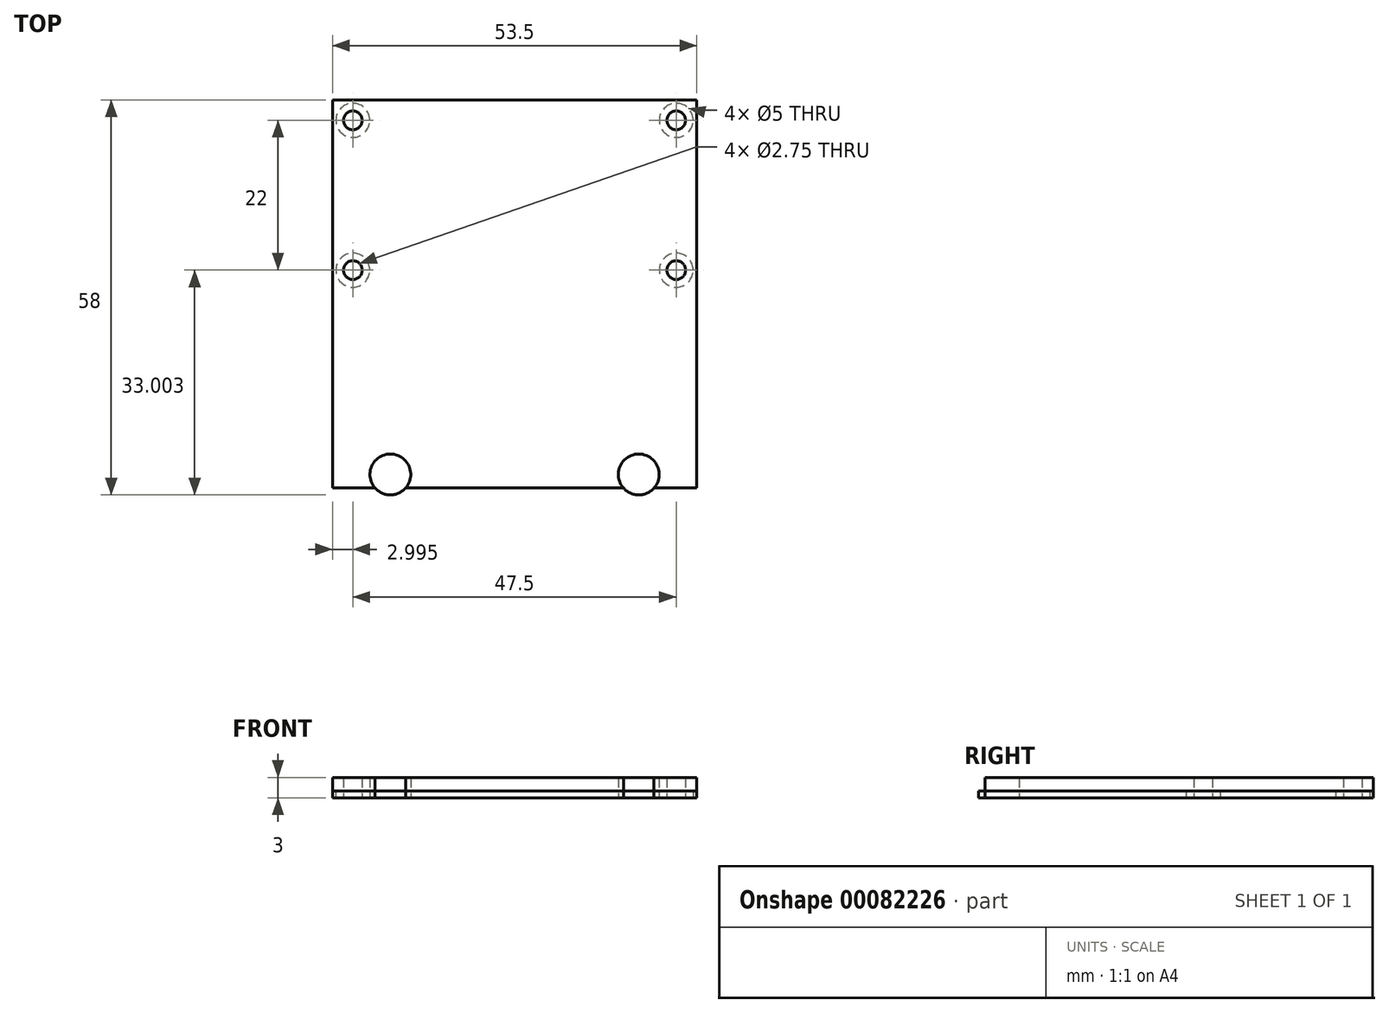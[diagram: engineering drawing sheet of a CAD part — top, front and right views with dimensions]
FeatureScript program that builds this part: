
annotation { "Feature Type Name" : "Feature", "Feature Type Description" : "" }
export const myFeature = defineFeature(function(context is Context, id is Id, definition is map)
    precondition{}
    {
        {
            var Q0;
            Q0=qCreatedBy(makeId("Top.planeOp"),FACE);
            var sketch = newSketch(context, id + "F0", { "sketchPlane" : qUnion([Q0])});
            skLineSegment(sketch, "E0.bottom", {"start": v(-25.28, 28.67) * mm, "end": v(28.22, 28.67) * mm});
            skLineSegment(sketch, "E0.top", {"start": v(-25.28, -28.33) * mm, "end": v(28.22, -28.33) * mm});
            skLineSegment(sketch, "E0.left", {"start": v(-25.28, 28.67) * mm, "end": v(-25.28, -28.33) * mm});
            skLineSegment(sketch, "E0.right", {"start": v(28.22, 28.67) * mm, "end": v(28.22, -28.33) * mm});
            skCircle(sketch, "E1", {"center": v(-22.28, 25.67) * mm, "radius": 1.38 * mm});
            skCircle(sketch, "E2", {"center": v(25.22, 25.67) * mm, "radius": 1.38 * mm});
            skCircle(sketch, "E3", {"center": v(-22.28, 3.67) * mm, "radius": 1.38 * mm});
            skCircle(sketch, "E4", {"center": v(25.22, 3.67) * mm, "radius": 1.38 * mm});
            skCircle(sketch, "E5", {"center": v(-22.28, 3.67) * mm, "radius": 2.5 * mm});
            skCircle(sketch, "E6", {"center": v(-22.28, 25.67) * mm, "radius": 2.5 * mm});
            skCircle(sketch, "E7", {"center": v(25.22, 25.67) * mm, "radius": 2.5 * mm});
            skCircle(sketch, "E8", {"center": v(25.22, 3.67) * mm, "radius": 2.5 * mm});
            skCircle(sketch, "E9", {"center": v(19.72, -26.33) * mm, "radius": 3 * mm});
            skCircle(sketch, "E10", {"center": v(-16.78, -26.33) * mm, "radius": 3 * mm});
            skSolve(sketch);
        }
        {
            var Q0;
            Q0=makeQuery(id+"F0.imprint","IMPRINT",FACE,{"disambiguationData":[TD([[makeQuery(id+"F0.imprint","IMPRINT",EDGE,{"derivedFrom":sQuery(id+"F0.wireOp",EDGE,"E1")}),-1.0]])]});
            var Q1;
            Q1=makeQuery(id+"F0.imprint","IMPRINT",FACE,{"disambiguationData":[TD([[makeQuery(id+"F0.imprint","IMPRINT",EDGE,{"derivedFrom":sQuery(id+"F0.wireOp",EDGE,"E3")}),-1.0]])]});
            var Q2;
            Q2=makeQuery(id+"F0.imprint","IMPRINT",FACE,{"disambiguationData":[TD([[makeQuery(id+"F0.imprint","IMPRINT",EDGE,{"derivedFrom":sQuery(id+"F0.wireOp",EDGE,"E4")}),-1.0]])]});
            var Q3;
            Q3=makeQuery(id+"F0.imprint","IMPRINT",FACE,{"disambiguationData":[TD([[makeQuery(id+"F0.imprint","IMPRINT",EDGE,{"derivedFrom":sQuery(id+"F0.wireOp",EDGE,"E2")}),-1.0]])]});
            var Q4;
            {var subQ0=sQuery(id+"F0.wireOp",EDGE,"E10");var subQ1=sQuery(id+"F0.wireOp",EDGE,"E0.top");var subQ2=makeQuery(id+"F0.imprint","INTERSECT",VERTEX,{"disambiguationData":[OD(0.0)],"derivedFrom":[subQ1,subQ0]});Q4=makeQuery(id+"F0.imprint","IMPRINT",FACE,{"disambiguationData":[TD([[makeQuery(id+"F0.imprint","IMPRINT",EDGE,{"disambiguationData":[TD([[subQ2,-1.0]])],"derivedFrom":subQ1}),1.0]])]});}
            var Q5;
            {var subQ0=sQuery(id+"F0.wireOp",EDGE,"E9");var subQ1=sQuery(id+"F0.wireOp",EDGE,"E0.top");var subQ2=makeQuery(id+"F0.imprint","INTERSECT",VERTEX,{"disambiguationData":[OD(0.0)],"derivedFrom":[subQ1,subQ0]});Q5=makeQuery(id+"F0.imprint","IMPRINT",FACE,{"disambiguationData":[TD([[makeQuery(id+"F0.imprint","IMPRINT",EDGE,{"disambiguationData":[TD([[subQ2,-1.0]])],"derivedFrom":subQ1}),1.0]])]});}
            extrude(context, id + "F1", {"entities" : qUnion([Q0, Q1, Q2, Q3, Q4, Q5]), "depth" : 3 * mm});
        }
        {
            var Q0;
            Q0 = qSketchRegion(id + "F0", true);
            extrude(context, id + "F2", {"entities" : qUnion([Q0]), "depth" : 1 * mm});
        }
    });
